FCSTD DOCUMENT  (FreeCAD 0.16R6706 (Git))
Label: body
License: All rights reserved
LicenseURL: http://en.wikipedia.org/wiki/All_rights_reserved
objects: Sketcher::SketchObject×1
note: 1 computed .brp shape members not serialized (recipe doc carries the construction recipe); baked Part::Feature solids carry a one-line shape summary decoded from their .brp

FEATURE [Sketcher::SketchObject] Sketch
  sketch-geometry (62):
    g0: ArcOfCircle CenterX=0 CenterY=0 CenterZ=0 NormalX=0 NormalY=0 NormalZ=1 Radius=54.3492 StartAngle=0.909764 EndAngle=2.23183
    g1: ArcOfCircle CenterX=44.4175 CenterY=57.1095 CenterZ=0 NormalX=0 NormalY=0 NormalZ=1 Radius=18 StartAngle=4.05136 EndAngle=7.19295
    g2: ArcOfCircle CenterX=-44.4175 CenterY=57.1095 CenterZ=0 NormalX=0 NormalY=0 NormalZ=1 Radius=18 StartAngle=2.23183 EndAngle=5.37342
    g3: ArcOfCircle CenterX=67.7469 CenterY=87.1051 CenterZ=0 NormalX=0 NormalY=0 NormalZ=1 Radius=20 StartAngle=1.49641 EndAngle=4.05136
    g4: ArcOfCircle CenterX=-67.7469 CenterY=87.1051 CenterZ=0 NormalX=0 NormalY=0 NormalZ=1 Radius=20 StartAngle=5.37342 EndAngle=7.92837
    g5: ArcOfCircle CenterX=70.5711 CenterY=125 CenterZ=0 NormalX=0 NormalY=0 NormalZ=1 Radius=18 StartAngle=4.638 EndAngle=7.92837
    g6: ArcOfCircle CenterX=-70.5711 CenterY=125 CenterZ=0 NormalX=0 NormalY=0 NormalZ=1 Radius=18 StartAngle=1.49641 EndAngle=4.78678
    g7: ArcOfCircle CenterX=67.7469 CenterY=162.895 CenterZ=0 NormalX=0 NormalY=0 NormalZ=1 Radius=20 StartAngle=2.23183 EndAngle=4.78678
    g8: ArcOfCircle CenterX=-67.7469 CenterY=162.895 CenterZ=0 NormalX=0 NormalY=0 NormalZ=1 Radius=20 StartAngle=4.638 EndAngle=7.19295
    g9: ArcOfCircle CenterX=44.4175 CenterY=192.891 CenterZ=0 NormalX=0 NormalY=0 NormalZ=1 Radius=18 StartAngle=5.37342 EndAngle=8.51501
    g10: ArcOfCircle CenterX=-44.4175 CenterY=192.891 CenterZ=0 NormalX=0 NormalY=0 NormalZ=1 Radius=18 StartAngle=0.909762 EndAngle=4.05136
    g11: ArcOfCircle CenterX=0 CenterY=250 CenterZ=0 NormalX=0 NormalY=0 NormalZ=1 Radius=54.3492 StartAngle=4.05136 EndAngle=5.37342
    g12: GeomPoint [constr] X=0 Y=57.1095 Z=0
    g13: GeomPoint [constr] X=0 Y=192.891 Z=0
    g14: GeomPoint [constr] X=0 Y=125 Z=0
    g15: LineSegment StartX=76.5711 StartY=131 StartZ=0 EndX=76.5711 EndY=119 EndZ=0
    g16: LineSegment StartX=76.5711 StartY=119 StartZ=0 EndX=53.5711 EndY=119 EndZ=0
    g17: LineSegment StartX=53.5711 StartY=119 StartZ=0 EndX=53.5711 EndY=131 EndZ=0
    g18: LineSegment StartX=53.5711 StartY=131 StartZ=0 EndX=76.5711 EndY=131 EndZ=0
    g19: GeomPoint [constr] X=70.5711 Y=125 Z=0
    g20: Circle CenterX=78.8711 CenterY=125 CenterZ=0 NormalX=0 NormalY=0 NormalZ=1 Radius=1.5
    g21: Circle CenterX=51.2711 CenterY=125 CenterZ=0 NormalX=0 NormalY=0 NormalZ=1 Radius=1.5
    g22: LineSegment StartX=52.8373 StartY=58.162 StartZ=0 EndX=45.4701 EndY=48.6897 EndZ=0
    g23: LineSegment StartX=45.4701 StartY=48.6897 StartZ=0 EndX=27.3148 EndY=62.8102 EndZ=0
    g24: LineSegment StartX=27.3148 StartY=62.8102 StartZ=0 EndX=34.682 EndY=72.2825 EndZ=0
    g25: LineSegment StartX=34.682 StartY=72.2825 StartZ=0 EndX=52.8373 EndY=58.162 EndZ=0
    g26: GeomPoint [constr] X=44.4175 Y=57.1095 Z=0
    g27: Circle CenterX=50.9692 CenterY=52.0138 CenterZ=0 NormalX=0 NormalY=0 NormalZ=1 Radius=1.5
    g28: Circle CenterX=29.1829 CenterY=68.9584 CenterZ=0 NormalX=0 NormalY=0 NormalZ=1 Radius=1.5
    g29: GeomPoint [constr] X=44.4175 Y=57.1095 Z=0
    g30: LineSegment StartX=-45.4701 StartY=48.6897 StartZ=0 EndX=-52.8373 EndY=58.162 EndZ=0
    g31: LineSegment StartX=-52.8373 StartY=58.162 StartZ=0 EndX=-34.682 EndY=72.2825 EndZ=0
    g32: LineSegment StartX=-34.682 StartY=72.2825 StartZ=0 EndX=-27.3148 EndY=62.8102 EndZ=0
    g33: LineSegment StartX=-27.3148 StartY=62.8102 StartZ=0 EndX=-45.4701 EndY=48.6897 EndZ=0
    g34: GeomPoint [constr] X=-44.4175 Y=57.1095 Z=0
    g35: Circle CenterX=-50.9692 CenterY=52.0138 CenterZ=0 NormalX=0 NormalY=0 NormalZ=1 Radius=1.5
    g36: Circle CenterX=-29.1829 CenterY=68.9584 CenterZ=0 NormalX=0 NormalY=0 NormalZ=1 Radius=1.5
    g37: GeomPoint [constr] X=-44.4175 Y=57.1095 Z=0
    g38: LineSegment StartX=45.1016 StartY=201.348 StartZ=0 EndX=52.8752 EndY=192.206 EndZ=0
    g39: LineSegment StartX=52.8752 StartY=192.206 StartZ=0 EndX=35.3535 EndY=177.307 EndZ=0
    g40: LineSegment StartX=35.3535 StartY=177.307 StartZ=0 EndX=27.5799 EndY=186.449 EndZ=0
    g41: LineSegment StartX=27.5799 StartY=186.449 StartZ=0 EndX=45.1016 EndY=201.348 EndZ=0
    g42: GeomPoint [constr] X=44.4175 Y=192.891 Z=0
    g43: Circle CenterX=50.7405 CenterY=198.267 CenterZ=0 NormalX=0 NormalY=0 NormalZ=1 Radius=1.5
    g44: Circle CenterX=29.7145 CenterY=180.388 CenterZ=0 NormalX=0 NormalY=0 NormalZ=1 Radius=1.5
    g45: GeomPoint [constr] X=44.4175 Y=192.891 Z=0
    g46: LineSegment StartX=-76.5711 StartY=119 StartZ=0 EndX=-76.5711 EndY=131 EndZ=0
    g47: LineSegment StartX=-76.5711 StartY=131 StartZ=0 EndX=-53.5711 EndY=131 EndZ=0
    g48: LineSegment StartX=-53.5711 StartY=131 StartZ=0 EndX=-53.5711 EndY=119 EndZ=0
    g49: LineSegment StartX=-53.5711 StartY=119 StartZ=0 EndX=-76.5711 EndY=119 EndZ=0
    g50: GeomPoint [constr] X=-70.5711 Y=125 Z=0
    g51: Circle CenterX=-78.8711 CenterY=125 CenterZ=0 NormalX=0 NormalY=0 NormalZ=1 Radius=1.5
    g52: Circle CenterX=-51.2711 CenterY=125 CenterZ=0 NormalX=0 NormalY=0 NormalZ=1 Radius=1.5
    g53: LineSegment StartX=-52.8768 StartY=192.227 StartZ=0 EndX=-45.0813 EndY=201.35 EndZ=0
    g54: LineSegment StartX=-45.0813 StartY=201.35 StartZ=0 EndX=-27.5954 EndY=186.408 EndZ=0
    g55: LineSegment StartX=-27.5954 StartY=186.408 StartZ=0 EndX=-35.3909 EndY=177.285 EndZ=0
    g56: LineSegment StartX=-35.3909 StartY=177.285 StartZ=0 EndX=-52.8768 EndY=192.227 EndZ=0
    g57: GeomPoint [constr] X=-44.4175 Y=192.891 Z=0
    g58: Circle CenterX=-50.7276 CenterY=198.282 CenterZ=0 NormalX=0 NormalY=0 NormalZ=1 Radius=1.5
    g59: Circle CenterX=-29.7446 CenterY=180.353 CenterZ=0 NormalX=0 NormalY=0 NormalZ=1 Radius=1.5
    g60: GeomPoint [constr] X=-44.4175 Y=192.891 Z=0
    g61: GeomPoint [constr] X=-41.8916 Y=190.732 Z=0
  constraints (158):
    c: Coincident(g0,g-1)
    c: Coincident(g1,g0)
    c: Coincident(g2,g0)
    c: Tangent(g2,g0)
    c: Tangent(g1,g0)
    c: Coincident(g3,g1)
    c: Coincident(g4,g2)
    c: Tangent(g4,g2)
    c: Tangent(g3,g1)
    c: Coincident(g5,g3)
    c: Coincident(g6,g4)
    c: Tangent(g4,g6)
    c: Tangent(g5,g3)
    c: Symmetric(g3,g4,g-2)
    c: Coincident(g7,g5)
    c: Coincident(g6,g8)
    c: Tangent(g6,g8)
    c: Tangent(g5,g7)
    c: Symmetric(g7,g8,g-2)
    c: Coincident(g9,g7)
    c: Tangent(g10,g8)
    c: Tangent(g7,g9)
    c: PointOnObject(g11,g-2)
    c: Coincident(g10,g11)
    c: Coincident(g9,g11)
    c: Radius(g9) = 18
    c: Tangent(g9,g11)
    c: Radius(g5) = 18
    c: Radius(g1) = 18
    c: DistanceX(g1,g9) = 0
    c: Tangent(g11,g10)
    c: PointOnObject(g12,g-2)
    c: PointOnObject(g13,g-2)
    c: Symmetric(g9,g10,g13)
    c: Symmetric(g1,g2,g12)
    c: Equal(g11,g0)
    c: DistanceY(g0,g0) = 0
    c: Equal(g7,g3)
    c: Symmetric(g5,g6,g14)
    c: Symmetric(g12,g13,g14)
    c: Symmetric(g10,g9,g-2)
    c: DistanceY(g11) = 250
    c: Coincident(g15,g16)
    c: Coincident(g16,g17)
    c: Coincident(g17,g18)
    c: Coincident(g18,g15)
    c: Parallel(g16,g18)
    c: Perpendicular(g18,g15)
    c: Parallel(g17,g15)
    c: Distance(g17,g15) = 23
    c: Distance(g15,g18) = 12
    c: Distance(g19,g16) = 6
    c: Distance(g19,g15) = 6
    c: Radius(g20) = 1.5
    c: Distance(g20,g15) = 2.3
    c: Distance(g20,g16) = 6
    c: Radius(g21) = 1.5
    c: Distance(g21,g16) = 6
    c: Distance(g21,g17) = 2.3
    c: Coincident(g5,g19)
    c: Horizontal(g16)
    c: Coincident(g22,g23)
    c: Coincident(g23,g24)
    c: Coincident(g24,g25)
    c: Coincident(g25,g22)
    c: Parallel(g23,g25)
    c: Perpendicular(g25,g22)
    c: Parallel(g24,g22)
    c: Distance(g24,g22) = 23
    c: Distance(g22,g25) = 12
    c: Distance(g26,g23) = 6
    c: Distance(g26,g22) = 6
    c: Radius(g27) = 1.5
    c: Distance(g27,g22) = 2.3
    c: Distance(g27,g23) = 6
    c: Radius(g28) = 1.5
    c: Distance(g28,g23) = 6
    c: Distance(g28,g24) = 2.3
    c: Coincident(g1,g26)
    c: Symmetric(g0,g1,g29)
    c: Coincident(g30,g31)
    c: Coincident(g31,g32)
    c: Coincident(g32,g33)
    c: Coincident(g33,g30)
    c: Parallel(g31,g33)
    c: Perpendicular(g33,g30)
    c: Parallel(g32,g30)
    c: Distance(g32,g30) = 23
    c: Distance(g30,g33) = 12
    c: Distance(g34,g31) = 6
    c: Distance(g34,g30) = 6
    c: Radius(g35) = 1.5
    c: Distance(g35,g30) = 2.3
    c: Distance(g35,g31) = 6
    c: Radius(g36) = 1.5
    c: Distance(g36,g31) = 6
    c: Distance(g36,g32) = 2.3
    c: Distance(g37,g31) = 6
    c: Coincident(g2,g34)
    c: Symmetric(g0,g2,g37)
    c: Coincident(g38,g39)
    c: Coincident(g39,g40)
    c: Coincident(g40,g41)
    c: Coincident(g41,g38)
    c: Parallel(g39,g41)
    c: Perpendicular(g41,g38)
    c: Parallel(g40,g38)
    c: Distance(g40,g38) = 23
    c: Distance(g38,g41) = 12
    c: Distance(g42,g39) = 6
    c: Distance(g42,g38) = 6
    c: Radius(g43) = 1.5
    c: Distance(g43,g38) = 2.3
    c: Distance(g43,g39) = 6
    c: Radius(g44) = 1.5
    c: Distance(g44,g39) = 6
    c: Distance(g44,g40) = 2.3
    c: Symmetric(g7,g9,g45)
    c: Coincident(g42,g9)
    c: Radius(g7) = 20
    c: Coincident(g46,g47)
    c: Coincident(g47,g48)
    c: Coincident(g48,g49)
    c: Coincident(g49,g46)
    c: Parallel(g47,g49)
    c: Perpendicular(g49,g46)
    c: Parallel(g48,g46)
    c: Distance(g48,g46) = 23
    c: Distance(g46,g49) = 12
    c: Distance(g50,g47) = 6
    c: Distance(g50,g46) = 6
    c: Radius(g51) = 1.5
    c: Distance(g51,g46) = 2.3
    c: Distance(g51,g47) = 6
    c: Radius(g52) = 1.5
    c: Distance(g52,g47) = 6
    c: Distance(g52,g48) = 2.3
    c: Horizontal(g47)
    c: Coincident(g6,g50)
    c: Coincident(g8,g10)
    c: Coincident(g53,g54)
    c: Coincident(g54,g55)
    c: Coincident(g55,g56)
    c: Coincident(g56,g53)
    c: Parallel(g54,g56)
    c: Perpendicular(g56,g53)
    c: Parallel(g55,g53)
    c: Distance(g55,g53) = 23
    c: Distance(g53,g56) = 12
    c: Distance(g57,g54) = 6
    c: Distance(g57,g53) = 6
    c: Radius(g58) = 1.5
    c: Distance(g58,g53) = 2.3
    c: Distance(g58,g54) = 6
    c: Radius(g59) = 1.5
    c: Distance(g59,g54) = 6
    c: Distance(g59,g55) = 2.3
    c: Distance(g61,g54) = 6
